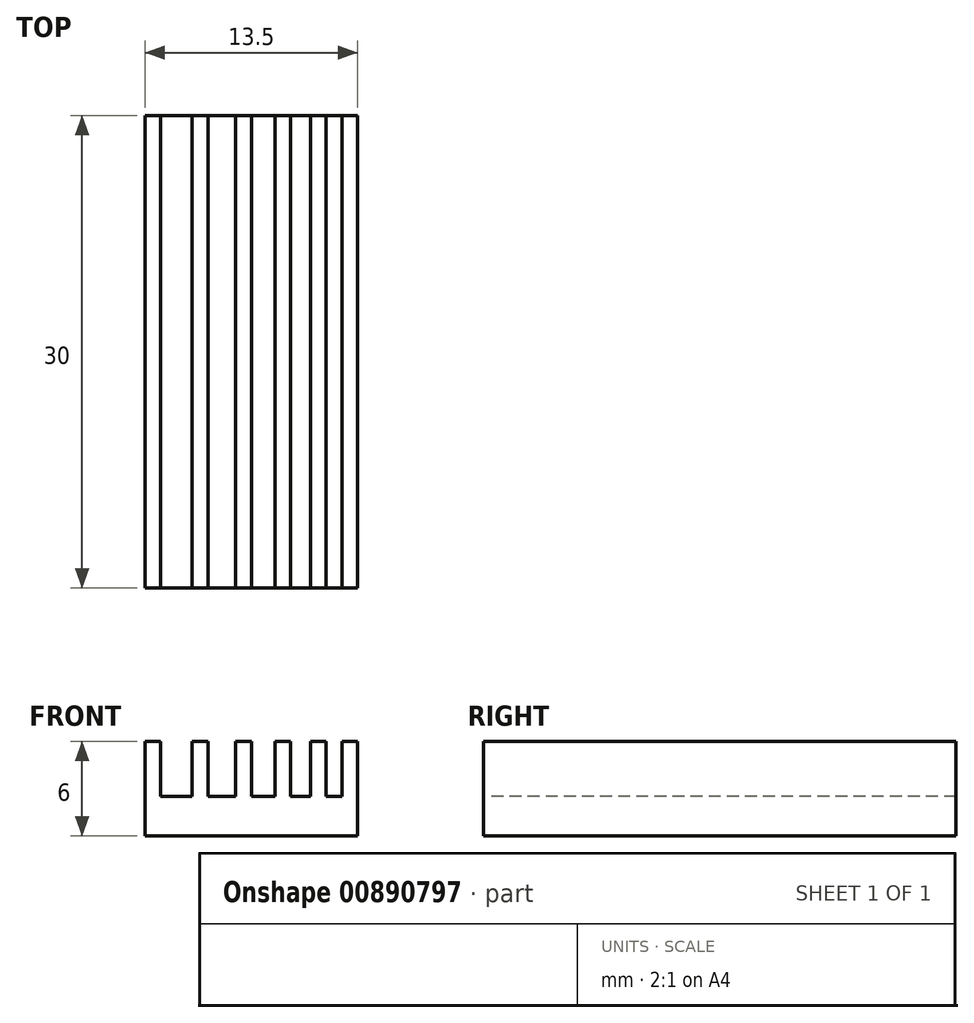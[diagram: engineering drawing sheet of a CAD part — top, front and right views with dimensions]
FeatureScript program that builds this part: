
annotation { "Feature Type Name" : "Feature", "Feature Type Description" : "" }
export const myFeature = defineFeature(function(context is Context, id is Id, definition is map)
    precondition{}
    {
        {
            var Q0;
            Q0=qCreatedBy(makeId("Top.planeOp"),FACE);
            var sketch = newSketch(context, id + "F0", { "sketchPlane" : qUnion([Q0])});
            skLineSegment(sketch, "E0.bottom", {"start": v(-46.31, 50.66) * mm, "end": v(53.69, 50.66) * mm});
            skLineSegment(sketch, "E0.top", {"start": v(-46.31, -49.34) * mm, "end": v(53.69, -49.34) * mm});
            skLineSegment(sketch, "E0.left", {"start": v(-46.31, 50.66) * mm, "end": v(-46.31, -49.34) * mm});
            skLineSegment(sketch, "E0.right", {"start": v(53.69, 50.66) * mm, "end": v(53.69, -49.34) * mm});
            skSolve(sketch);
        }
        {
            var Q0;
            Q0 = qSketchRegion(id + "F0", true);
            extrude(context, id + "F1", {"entities" : qUnion([Q0]), "depth" : 6 * mm, "offsetDistance" : 25 * mm});
        }
        {
            var Q0;
            Q0=makeQuery(id+"F1.opExtrude","CAP_FACE",FACE,{"disambiguationData":[OSD([sQuery(id+"F0.wireOp",EDGE,"E0.bottom"),sQuery(id+"F0.wireOp",EDGE,"E0.top"),sQuery(id+"F0.wireOp",EDGE,"E0.left"),sQuery(id+"F0.wireOp",EDGE,"E0.right")])],"isStart":false});
            var sketch = newSketch(context, id + "F2", { "sketchPlane" : qUnion([Q0])});
            skLineSegment(sketch, "E1.bottom", {"start": v(-45.31, 50.66) * mm, "end": v(-43.31, 50.66) * mm});
            skLineSegment(sketch, "E1.top", {"start": v(-45.31, -49.34) * mm, "end": v(-43.31, -49.34) * mm});
            skLineSegment(sketch, "E1.left", {"start": v(-45.31, 50.66) * mm, "end": v(-45.31, -49.34) * mm});
            skLineSegment(sketch, "E1.right", {"start": v(-43.31, 50.66) * mm, "end": v(-43.31, -49.34) * mm});
            skLineSegment(sketch, "E2.bottom", {"start": v(-42.31, 50.66) * mm, "end": v(-40.56, 50.66) * mm});
            skLineSegment(sketch, "E2.top", {"start": v(-42.31, -49.34) * mm, "end": v(-40.56, -49.34) * mm});
            skLineSegment(sketch, "E2.left", {"start": v(-42.31, 50.66) * mm, "end": v(-42.31, -49.34) * mm});
            skLineSegment(sketch, "E2.right", {"start": v(-40.56, 50.66) * mm, "end": v(-40.56, -49.34) * mm});
            skLineSegment(sketch, "E3.bottom", {"start": v(-39.56, 50.66) * mm, "end": v(-38.06, 50.66) * mm});
            skLineSegment(sketch, "E3.top", {"start": v(-39.56, -49.34) * mm, "end": v(-38.06, -49.34) * mm});
            skLineSegment(sketch, "E3.left", {"start": v(-39.56, 50.66) * mm, "end": v(-39.56, -49.34) * mm});
            skLineSegment(sketch, "E3.right", {"start": v(-38.06, 50.66) * mm, "end": v(-38.06, -49.34) * mm});
            skLineSegment(sketch, "E4.bottom", {"start": v(-37.06, 50.66) * mm, "end": v(-35.81, 50.66) * mm});
            skLineSegment(sketch, "E4.top", {"start": v(-37.06, -49.34) * mm, "end": v(-35.81, -49.34) * mm});
            skLineSegment(sketch, "E4.left", {"start": v(-37.06, 50.66) * mm, "end": v(-37.06, -49.34) * mm});
            skLineSegment(sketch, "E4.right", {"start": v(-35.81, 50.66) * mm, "end": v(-35.81, -49.34) * mm});
            skLineSegment(sketch, "E5.bottom", {"start": v(-34.81, 50.66) * mm, "end": v(-33.81, 50.66) * mm});
            skLineSegment(sketch, "E5.top", {"start": v(-34.81, -49.34) * mm, "end": v(-33.81, -49.34) * mm});
            skLineSegment(sketch, "E5.left", {"start": v(-34.81, 50.66) * mm, "end": v(-34.81, -49.34) * mm});
            skLineSegment(sketch, "E5.right", {"start": v(-33.81, 50.66) * mm, "end": v(-33.81, -49.34) * mm});
            skSolve(sketch);
        }
        {
            var Q0;
            Q0 = qSketchRegion(id + "F2", true);
            extrude(context, id + "F3", {"entities" : qUnion([Q0]), "operationType" : NewBodyOperationType.REMOVE, "oppositeDirection" : true, "depth" : 3.5 * mm, "offsetDistance" : 25 * mm});
        }
        {
            var Q0;
            {var subQ0=sQuery(id+"F0.wireOp",EDGE,"E0.bottom");var subQ1=sQuery(id+"F0.wireOp",EDGE,"E0.right");var subQ2=sQuery(id+"F0.wireOp",EDGE,"E0.top");Q0=makeQuery(id+"F3.boolean.opBoolean","SPLIT",FACE,{"disambiguationData":[TD([makeQuery(id+"F1.opExtrude","SWEPT_FACE",FACE,{"disambiguationData":[OSD([subQ1])]})])],"derivedFrom":makeQuery(id+"F1.opExtrude","CAP_FACE",FACE,{"disambiguationData":[OSD([subQ0,subQ2,sQuery(id+"F0.wireOp",EDGE,"E0.left"),subQ1])],"isStart":false})});}
            var sketch = newSketch(context, id + "F4", { "sketchPlane" : qUnion([Q0])});
            skLineSegment(sketch, "E6.bottom", {"start": v(-32.81, 50.66) * mm, "end": v(53.69, 50.66) * mm});
            skLineSegment(sketch, "E6.top", {"start": v(-32.81, -49.34) * mm, "end": v(53.69, -49.34) * mm});
            skLineSegment(sketch, "E6.left", {"start": v(-32.81, 50.66) * mm, "end": v(-32.81, -49.34) * mm});
            skLineSegment(sketch, "E6.right", {"start": v(53.69, 50.66) * mm, "end": v(53.69, -49.34) * mm});
            skSolve(sketch);
        }
        {
            var Q0;
            Q0 = qSketchRegion(id + "F4", true);
            extrude(context, id + "F5", {"entities" : qUnion([Q0]), "operationType" : NewBodyOperationType.REMOVE, "oppositeDirection" : true, "depth" : 25 * mm, "offsetDistance" : 25 * mm});
        }
        {
            var Q0;
            Q0=makeQuery(id+"F1.opExtrude","CAP_FACE",FACE,{"disambiguationData":[OSD([sQuery(id+"F0.wireOp",EDGE,"E0.bottom"),sQuery(id+"F0.wireOp",EDGE,"E0.top"),sQuery(id+"F0.wireOp",EDGE,"E0.left"),sQuery(id+"F0.wireOp",EDGE,"E0.right")])],"isStart":true});
            var sketch = newSketch(context, id + "F6", { "sketchPlane" : qUnion([Q0])});
            skLineSegment(sketch, "E7.bottom", {"start": v(-46.31, 49.34) * mm, "end": v(-32.81, 49.34) * mm});
            skLineSegment(sketch, "E7.top", {"start": v(-46.31, -20.66) * mm, "end": v(-32.81, -20.66) * mm});
            skLineSegment(sketch, "E7.left", {"start": v(-46.31, 49.34) * mm, "end": v(-46.31, -20.66) * mm});
            skLineSegment(sketch, "E7.right", {"start": v(-32.81, 49.34) * mm, "end": v(-32.81, -20.66) * mm});
            skSolve(sketch);
        }
        {
            var Q0;
            Q0 = qSketchRegion(id + "F6", true);
            extrude(context, id + "F7", {"entities" : qUnion([Q0]), "operationType" : NewBodyOperationType.REMOVE, "oppositeDirection" : true, "depth" : 25 * mm, "offsetDistance" : 25 * mm});
        }
    });
